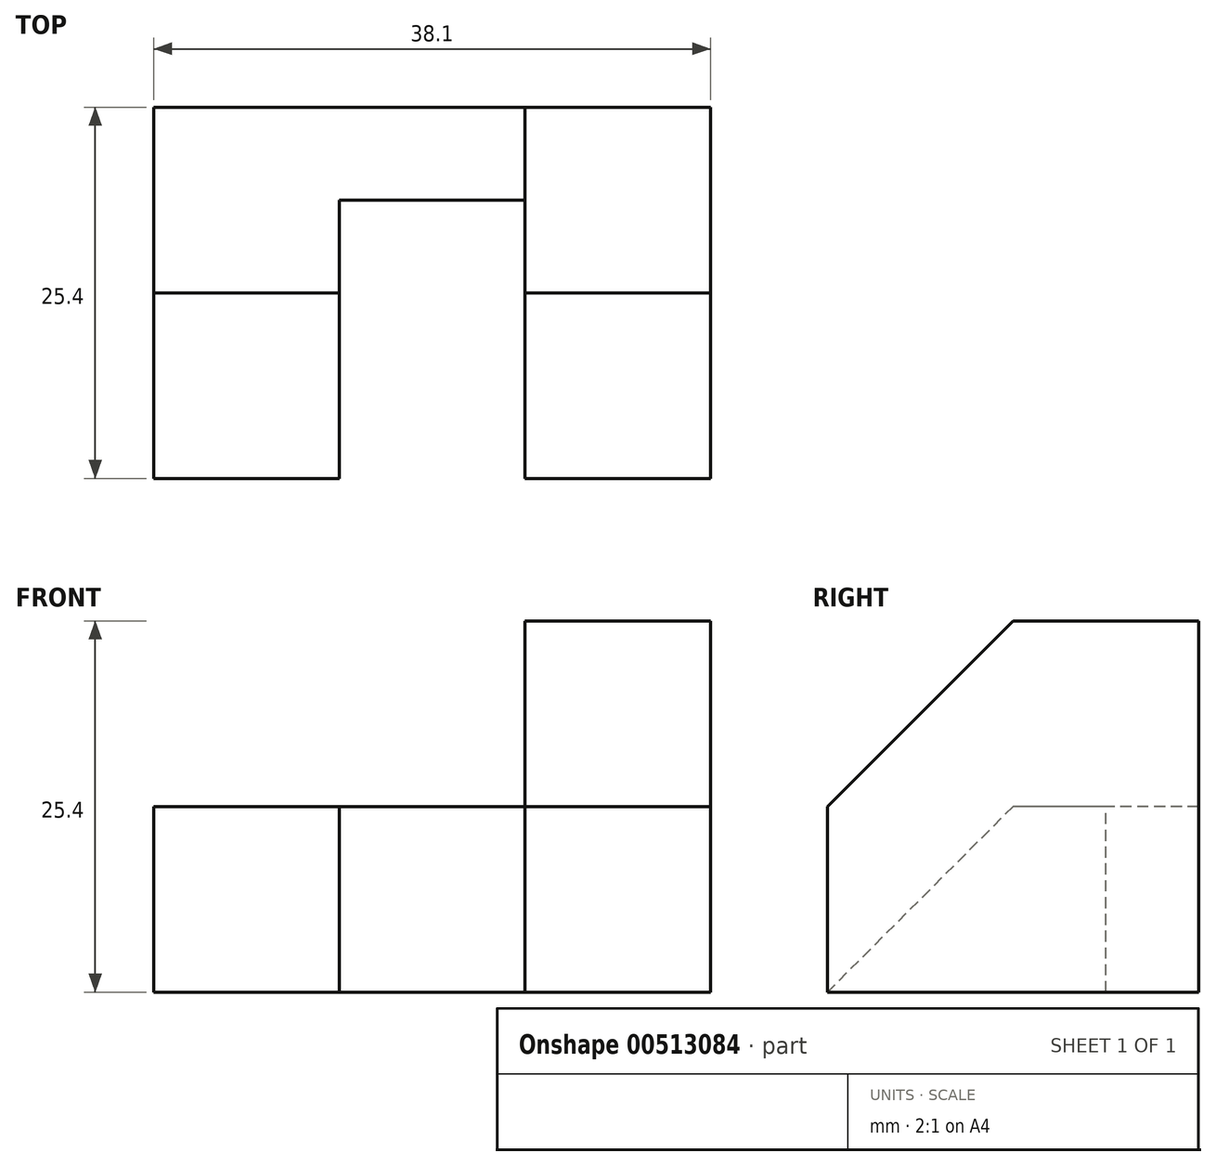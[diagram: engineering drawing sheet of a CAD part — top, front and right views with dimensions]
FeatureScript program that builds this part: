
annotation { "Feature Type Name" : "Feature", "Feature Type Description" : "" }
export const myFeature = defineFeature(function(context is Context, id is Id, definition is map)
    precondition{}
    {
        {
            var Q0;
            Q0=qCreatedBy(makeId("Right.planeOp"),FACE);
            var sketch = newSketch(context, id + "F0", { "sketchPlane" : qUnion([Q0])});
            skLineSegment(sketch, "E0", {"start": v(0, 0) * mm, "end": v(25.4, 0) * mm});
            skLineSegment(sketch, "E1", {"start": v(25.4, 0) * mm, "end": v(25.4, 25.4) * mm});
            skLineSegment(sketch, "E2", {"start": v(25.4, 25.4) * mm, "end": v(12.7, 25.4) * mm});
            skLineSegment(sketch, "E3", {"start": v(12.7, 25.4) * mm, "end": v(0, 12.7) * mm});
            skLineSegment(sketch, "E4", {"start": v(0, 12.7) * mm, "end": v(0, 0) * mm});
            skSolve(sketch);
        }
        {
            var Q0;
            Q0=makeQuery(id+"F0.imprint","IMPRINT",FACE,{"disambiguationData":[TD([[makeQuery(id+"F0.imprint","IMPRINT",EDGE,{"derivedFrom":sQuery(id+"F0.wireOp",EDGE,"E0")}),1.0]])]});
            extrude(context, id + "F1", {"entities" : qUnion([Q0]), "depth" : 12.7 * mm});
        }
        {
            var Q0;
            Q0=qCreatedBy(makeId("Right.planeOp"),FACE);
            var sketch = newSketch(context, id + "F2", { "sketchPlane" : qUnion([Q0])});
            skLineSegment(sketch, "E5", {"start": v(0, 0) * mm, "end": v(25.4, 0) * mm});
            skLineSegment(sketch, "E6", {"start": v(25.4, 0) * mm, "end": v(25.4, 12.7) * mm});
            skLineSegment(sketch, "E7", {"start": v(25.4, 12.7) * mm, "end": v(12.7, 12.7) * mm});
            skLineSegment(sketch, "E8", {"start": v(12.7, 12.7) * mm, "end": v(0, 0) * mm});
            skSolve(sketch);
        }
        {
            var Q0;
            Q0=qSketchRegion(id+"F2",true);
            extrude(context, id + "F3", {"entities" : qUnion([Q0]), "oppositeDirection" : true, "depth" : 25.4 * mm});
        }
        {
            var Q0;
            Q0=qCreatedBy(makeId("Right.planeOp"),FACE);
            var sketch = newSketch(context, id + "F4", { "sketchPlane" : qUnion([Q0])});
            skLineSegment(sketch, "E9", {"start": v(0, 0) * mm, "end": v(19.05, 0) * mm});
            skLineSegment(sketch, "E10", {"start": v(19.05, 0) * mm, "end": v(19.05, 12.7) * mm});
            skLineSegment(sketch, "E11", {"start": v(19.05, 12.7) * mm, "end": v(12.7, 12.7) * mm});
            skLineSegment(sketch, "E12", {"start": v(12.7, 12.7) * mm, "end": v(0, 0) * mm});
            skSolve(sketch);
        }
        {
            var Q0;
            Q0=qSketchRegion(id+"F4",true);
            extrude(context, id + "F5", {"entities" : qUnion([Q0]), "operationType" : NewBodyOperationType.REMOVE, "oppositeDirection" : true, "depth" : 12.7 * mm});
        }
    });
